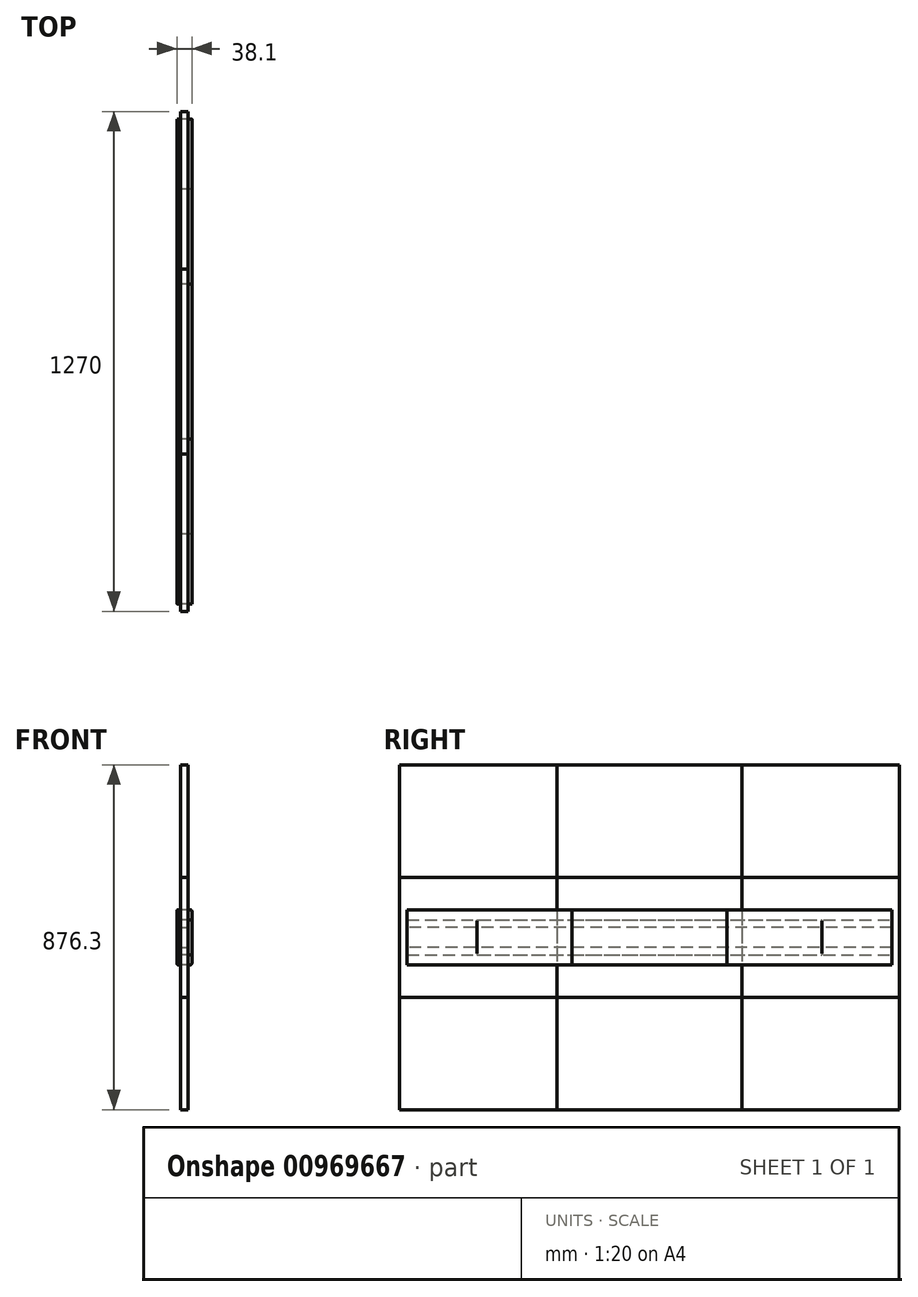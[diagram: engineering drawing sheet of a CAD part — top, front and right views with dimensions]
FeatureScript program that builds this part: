
annotation { "Feature Type Name" : "Feature", "Feature Type Description" : "" }
export const myFeature = defineFeature(function(context is Context, id is Id, definition is map)
    precondition{}
    {
        {
            var Q0;
            Q0=qCreatedBy(makeId("Front.planeOp"),FACE);
            var sketch = newSketch(context, id + "F0", { "sketchPlane" : qUnion([Q0])});
            skLineSegment(sketch, "E0.bottom", {"start": v(15.88, 69.85) * mm, "end": v(-15.87, 69.85) * mm});
            skLineSegment(sketch, "E0.top", {"start": v(15.88, -69.85) * mm, "end": v(-15.88, -69.85) * mm});
            skLineSegment(sketch, "E0.left", {"start": v(19.05, 66.67) * mm, "end": v(19.05, -66.68) * mm});
            skLineSegment(sketch, "E0.right", {"start": v(-19.05, 66.67) * mm, "end": v(-19.05, -66.68) * mm});
            skPoint(sketch, "E0.middle", {"position": v(0, 0) * mm});
            skPoint(sketch, "E1.visualSharp", {"position": v(-19.05, 69.85) * mm});
            skArc(sketch, "E1.filletArc", {"start": v(-15.87, 69.85) * mm, "mid": v(-18.12, 68.92) * mm, "end": v(-19.05, 66.67) * mm});
            skPoint(sketch, "E2.visualSharp", {"position": v(19.05, 69.85) * mm});
            skArc(sketch, "E2.filletArc", {"start": v(19.05, 66.67) * mm, "mid": v(18.12, 68.92) * mm, "end": v(15.88, 69.85) * mm});
            skPoint(sketch, "E3.visualSharp", {"position": v(19.05, -69.85) * mm});
            skArc(sketch, "E3.filletArc", {"start": v(15.88, -69.85) * mm, "mid": v(18.12, -68.92) * mm, "end": v(19.05, -66.68) * mm});
            skPoint(sketch, "E4.visualSharp", {"position": v(-19.05, -69.85) * mm});
            skArc(sketch, "E4.filletArc", {"start": v(-19.05, -66.68) * mm, "mid": v(-18.12, -68.92) * mm, "end": v(-15.88, -69.85) * mm});
            skSolve(sketch);
        }
        {
            var Q0;
            Q0=makeQuery(id+"F0.imprint","IMPRINT",FACE,{"disambiguationData":[TD([[makeQuery(id+"F0.imprint","IMPRINT",EDGE,{"derivedFrom":sQuery(id+"F0.wireOp",EDGE,"E0.bottom")}),1.0]])]});
            extrude(context, id + "F1", {"entities" : qUnion([Q0]), "endBound" : BoundingType.SYMMETRIC, "depth" : 393.7 * mm, "offsetDistance" : 25.4 * mm});
        }
        {
            var Q0;
            Q0 = qSketchRegion(id + "F0", true);
            extrude(context, id + "F2", {"entities" : qUnion([Q0]), "endBound" : BoundingType.SYMMETRIC, "depth" : 1231.9 * mm, "offsetDistance" : 25.4 * mm});
        }
        {
            var Q0;
            Q0=qCreatedBy(makeId("Front.planeOp"),FACE);
            var sketch = newSketch(context, id + "F3", { "sketchPlane" : qUnion([Q0])});
            skLineSegment(sketch, "E5.bottom", {"start": v(15.87, 44.45) * mm, "end": v(-15.88, 44.45) * mm});
            skLineSegment(sketch, "E5.top", {"start": v(15.87, -44.45) * mm, "end": v(-15.88, -44.45) * mm});
            skLineSegment(sketch, "E5.left", {"start": v(19.05, 41.28) * mm, "end": v(19.05, -41.27) * mm});
            skLineSegment(sketch, "E5.right", {"start": v(-19.05, 41.28) * mm, "end": v(-19.05, -41.27) * mm});
            skPoint(sketch, "E5.middle", {"position": v(0, 0) * mm});
            skPoint(sketch, "E6.visualSharp", {"position": v(-19.05, 44.45) * mm});
            skArc(sketch, "E6.filletArc", {"start": v(-15.88, 44.45) * mm, "mid": v(-18.12, 43.52) * mm, "end": v(-19.05, 41.28) * mm});
            skPoint(sketch, "E7.visualSharp", {"position": v(19.05, 44.45) * mm});
            skArc(sketch, "E7.filletArc", {"start": v(19.05, 41.28) * mm, "mid": v(18.12, 43.52) * mm, "end": v(15.87, 44.45) * mm});
            skPoint(sketch, "E8.visualSharp", {"position": v(19.05, -44.45) * mm});
            skArc(sketch, "E8.filletArc", {"start": v(15.87, -44.45) * mm, "mid": v(18.12, -43.52) * mm, "end": v(19.05, -41.27) * mm});
            skPoint(sketch, "E9.visualSharp", {"position": v(-19.05, -44.45) * mm});
            skArc(sketch, "E9.filletArc", {"start": v(-19.05, -41.27) * mm, "mid": v(-18.12, -43.52) * mm, "end": v(-15.88, -44.45) * mm});
            skSolve(sketch);
        }
        {
            var Q0;
            Q0 = qSketchRegion(id + "F3", true);
            var Q1;
            Q1=makeQuery(id+"F1.opExtrude","CAP_FACE",FACE,{"disambiguationData":[OSD([sQuery(id+"F0.wireOp",EDGE,"E0.bottom"),sQuery(id+"F0.wireOp",EDGE,"E0.top"),sQuery(id+"F0.wireOp",EDGE,"E0.left"),sQuery(id+"F0.wireOp",EDGE,"E0.right"),sQuery(id+"F0.wireOp",EDGE,"E1.filletArc"),sQuery(id+"F0.wireOp",EDGE,"E2.filletArc"),sQuery(id+"F0.wireOp",EDGE,"E3.filletArc"),sQuery(id+"F0.wireOp",EDGE,"E4.filletArc")])],"isStart":false});
            var Q2;
            Q2=makeQuery(id+"F1.opExtrude","CAP_FACE",FACE,{"disambiguationData":[OSD([sQuery(id+"F0.wireOp",EDGE,"E0.bottom"),sQuery(id+"F0.wireOp",EDGE,"E0.top"),sQuery(id+"F0.wireOp",EDGE,"E0.left"),sQuery(id+"F0.wireOp",EDGE,"E0.right"),sQuery(id+"F0.wireOp",EDGE,"E1.filletArc"),sQuery(id+"F0.wireOp",EDGE,"E2.filletArc"),sQuery(id+"F0.wireOp",EDGE,"E3.filletArc"),sQuery(id+"F0.wireOp",EDGE,"E4.filletArc")])],"isStart":true});
            extrude(context, id + "F4", {"entities" : qUnion([Q0]), "endBound" : BoundingType.UP_TO_SURFACE, "depth" : 25.4 * mm, "endBoundEntityFace" : qUnion([Q1]), "offsetDistance" : 25.4 * mm, "hasSecondDirection" : true, "secondDirectionBound" : SecondDirectionBoundingType.UP_TO_SURFACE, "secondDirectionOppositeDirection" : true, "secondDirectionDepth" : 25.4 * mm, "secondDirectionBoundEntityFace" : qUnion([Q2])});
        }
        {
            var Q0;
            Q0 = qSketchRegion(id + "F3", true);
            var Q1;
            Q1=makeQuery(id+"F2.opExtrude","CAP_FACE",FACE,{"disambiguationData":[OSD([sQuery(id+"F0.wireOp",EDGE,"E0.bottom"),sQuery(id+"F0.wireOp",EDGE,"E0.top"),sQuery(id+"F0.wireOp",EDGE,"E0.left"),sQuery(id+"F0.wireOp",EDGE,"E0.right"),sQuery(id+"F0.wireOp",EDGE,"E1.filletArc"),sQuery(id+"F0.wireOp",EDGE,"E2.filletArc"),sQuery(id+"F0.wireOp",EDGE,"E3.filletArc"),sQuery(id+"F0.wireOp",EDGE,"E4.filletArc")])],"isStart":false});
            var Q2;
            Q2=makeQuery(id+"F2.opExtrude","CAP_FACE",FACE,{"disambiguationData":[OSD([sQuery(id+"F0.wireOp",EDGE,"E0.bottom"),sQuery(id+"F0.wireOp",EDGE,"E0.top"),sQuery(id+"F0.wireOp",EDGE,"E0.left"),sQuery(id+"F0.wireOp",EDGE,"E0.right"),sQuery(id+"F0.wireOp",EDGE,"E1.filletArc"),sQuery(id+"F0.wireOp",EDGE,"E2.filletArc"),sQuery(id+"F0.wireOp",EDGE,"E3.filletArc"),sQuery(id+"F0.wireOp",EDGE,"E4.filletArc")])],"isStart":true});
            extrude(context, id + "F5", {"entities" : qUnion([Q0]), "endBound" : BoundingType.UP_TO_SURFACE, "depth" : 25.4 * mm, "endBoundEntityFace" : qUnion([Q1]), "offsetDistance" : 25.4 * mm, "hasSecondDirection" : true, "secondDirectionBound" : SecondDirectionBoundingType.UP_TO_SURFACE, "secondDirectionOppositeDirection" : true, "secondDirectionDepth" : 25.4 * mm, "secondDirectionBoundEntityFace" : qUnion([Q2])});
        }
        {
            assignVariable(context, id + "F6", {"variableType" : VariableType.LENGTH, "name" : "StandHeight", "lengthValue" : 914.4 * mm});
        }
        {
            var Q0;
            Q0 = qSketchRegion(id + "F3", true);
            extrude(context, id + "F7", {"entities" : qUnion([Q0]), "endBound" : BoundingType.SYMMETRIC, "depth" : getVariable(context, 'StandHeight') - 38.1 * mm, "offsetDistance" : 25.4 * mm});
        }
        {
            var Q0;
            Q0=qCreatedBy(makeId("Right.planeOp"),FACE);
            var sketch = newSketch(context, id + "F8", { "sketchPlane" : qUnion([Q0])});
            skLineSegment(sketch, "E10.bottom", {"start": v(-635, -438.15) * mm, "end": v(635, -438.15) * mm});
            skLineSegment(sketch, "E10.top", {"start": v(-635, 438.15) * mm, "end": v(635, 438.15) * mm});
            skLineSegment(sketch, "E10.left", {"start": v(-635, -438.15) * mm, "end": v(-635, 438.15) * mm});
            skLineSegment(sketch, "E10.right", {"start": v(635, -438.15) * mm, "end": v(635, 438.15) * mm});
            skPoint(sketch, "E10.middle", {"position": v(0, 0) * mm});
            skLineSegment(sketch, "E11.0", {"start": v(-615.95, 66.67) * mm, "end": v(-615.95, -66.68) * mm, "construction": true});
            skSolve(sketch);
        }
        {
            var Q0;
            Q0 = qSketchRegion(id + "F8", true);
            extrude(context, id + "F9", {"entities" : qUnion([Q0]), "endBound" : BoundingType.SYMMETRIC, "depth" : 19.05 * mm, "offsetDistance" : 25.4 * mm});
        }
        {
            var Q0;
            Q0=makeQuery(id+"F9.opExtrude","CAP_FACE",FACE,{"disambiguationData":[OSD([sQuery(id+"F8.wireOp",EDGE,"E10.bottom"),sQuery(id+"F8.wireOp",EDGE,"E10.top"),sQuery(id+"F8.wireOp",EDGE,"E10.left"),sQuery(id+"F8.wireOp",EDGE,"E10.right")])],"isStart":false});
            var sketch = newSketch(context, id + "F10", { "sketchPlane" : qUnion([Q0])});
            skLineSegment(sketch, "E12.bottom", {"start": v(-234.95, 438.15) * mm, "end": v(234.95, 438.15) * mm});
            skLineSegment(sketch, "E12.top", {"start": v(-234.95, -438.15) * mm, "end": v(234.95, -438.15) * mm});
            skLineSegment(sketch, "E12.left", {"start": v(-234.95, 438.15) * mm, "end": v(-234.95, -438.15) * mm});
            skLineSegment(sketch, "E12.right", {"start": v(234.95, 438.15) * mm, "end": v(234.95, -438.15) * mm});
            skSolve(sketch);
        }
        {
            var Q0;
            Q0 = qSketchRegion(id + "F10", true);
            extrude(context, id + "F11", {"entities" : qUnion([Q0]), "oppositeDirection" : true, "depth" : 19.05 * mm, "offsetDistance" : 25.4 * mm});
        }
        {
            var Q0;
            Q0=makeQuery(id+"F9.opExtrude","CAP_FACE",FACE,{"disambiguationData":[OSD([sQuery(id+"F8.wireOp",EDGE,"E10.bottom"),sQuery(id+"F8.wireOp",EDGE,"E10.top"),sQuery(id+"F8.wireOp",EDGE,"E10.left"),sQuery(id+"F8.wireOp",EDGE,"E10.right")])],"isStart":false});
            var sketch = newSketch(context, id + "F12", { "sketchPlane" : qUnion([Q0])});
            skLineSegment(sketch, "E13.bottom", {"start": v(635, 152.4) * mm, "end": v(-635, 152.4) * mm});
            skLineSegment(sketch, "E13.top", {"start": v(635, -152.4) * mm, "end": v(-635, -152.4) * mm});
            skLineSegment(sketch, "E13.left", {"start": v(635, 152.4) * mm, "end": v(635, -152.4) * mm});
            skLineSegment(sketch, "E13.right", {"start": v(-635, 152.4) * mm, "end": v(-635, -152.4) * mm});
            skPoint(sketch, "E13.middle", {"position": v(0, 0) * mm});
            skSolve(sketch);
        }
        {
            var Q0;
            Q0 = qSketchRegion(id + "F12", true);
            extrude(context, id + "F13", {"entities" : qUnion([Q0]), "oppositeDirection" : true, "depth" : 19.05 * mm, "offsetDistance" : 25.4 * mm});
        }
        {
            var Q0;
            Q0=makeQuery(id+"F9.opExtrude","CAP_FACE",FACE,{"disambiguationData":[OSD([sQuery(id+"F8.wireOp",EDGE,"E10.bottom"),sQuery(id+"F8.wireOp",EDGE,"E10.top"),sQuery(id+"F8.wireOp",EDGE,"E10.left"),sQuery(id+"F8.wireOp",EDGE,"E10.right")])],"isStart":false});
            var sketch = newSketch(context, id + "F14", { "sketchPlane" : qUnion([Q0])});
            skLineSegment(sketch, "E14.bottom", {"start": v(234.95, 152.4) * mm, "end": v(-234.95, 152.4) * mm});
            skLineSegment(sketch, "E14.top", {"start": v(234.95, -152.4) * mm, "end": v(-234.95, -152.4) * mm});
            skLineSegment(sketch, "E14.left", {"start": v(234.95, 152.4) * mm, "end": v(234.95, -152.4) * mm});
            skLineSegment(sketch, "E14.right", {"start": v(-234.95, 152.4) * mm, "end": v(-234.95, -152.4) * mm});
            skPoint(sketch, "E14.middle", {"position": v(0, 0) * mm});
            skSolve(sketch);
        }
        {
            var Q0;
            Q0 = qSketchRegion(id + "F14", true);
            extrude(context, id + "F15", {"entities" : qUnion([Q0]), "oppositeDirection" : true, "depth" : 19.05 * mm, "offsetDistance" : 25.4 * mm});
        }
        {
            var Q0;
            Q0=makeQuery(id+"F9.opExtrude","CAP_FACE",FACE,{"disambiguationData":[OSD([sQuery(id+"F8.wireOp",EDGE,"E10.bottom"),sQuery(id+"F8.wireOp",EDGE,"E10.top"),sQuery(id+"F8.wireOp",EDGE,"E10.left"),sQuery(id+"F8.wireOp",EDGE,"E10.right")])],"isStart":false});
            var sketch = newSketch(context, id + "F16", { "sketchPlane" : qUnion([Q0])});
            skLineSegment(sketch, "E15.bottom", {"start": v(615.95, 25.4) * mm, "end": v(-615.95, 25.4) * mm});
            skLineSegment(sketch, "E15.top", {"start": v(615.95, -25.4) * mm, "end": v(-615.95, -25.4) * mm});
            skLineSegment(sketch, "E15.left", {"start": v(615.95, 25.4) * mm, "end": v(615.95, -25.4) * mm});
            skLineSegment(sketch, "E15.right", {"start": v(-615.95, 25.4) * mm, "end": v(-615.95, -25.4) * mm});
            skPoint(sketch, "E15.middle", {"position": v(0, 0) * mm});
            skSolve(sketch);
        }
        {
            var Q0;
            Q0 = qSketchRegion(id + "F16", true);
            extrude(context, id + "F17", {"entities" : qUnion([Q0]), "oppositeDirection" : true, "depth" : 19.05 * mm, "offsetDistance" : 25.4 * mm});
        }
    });
